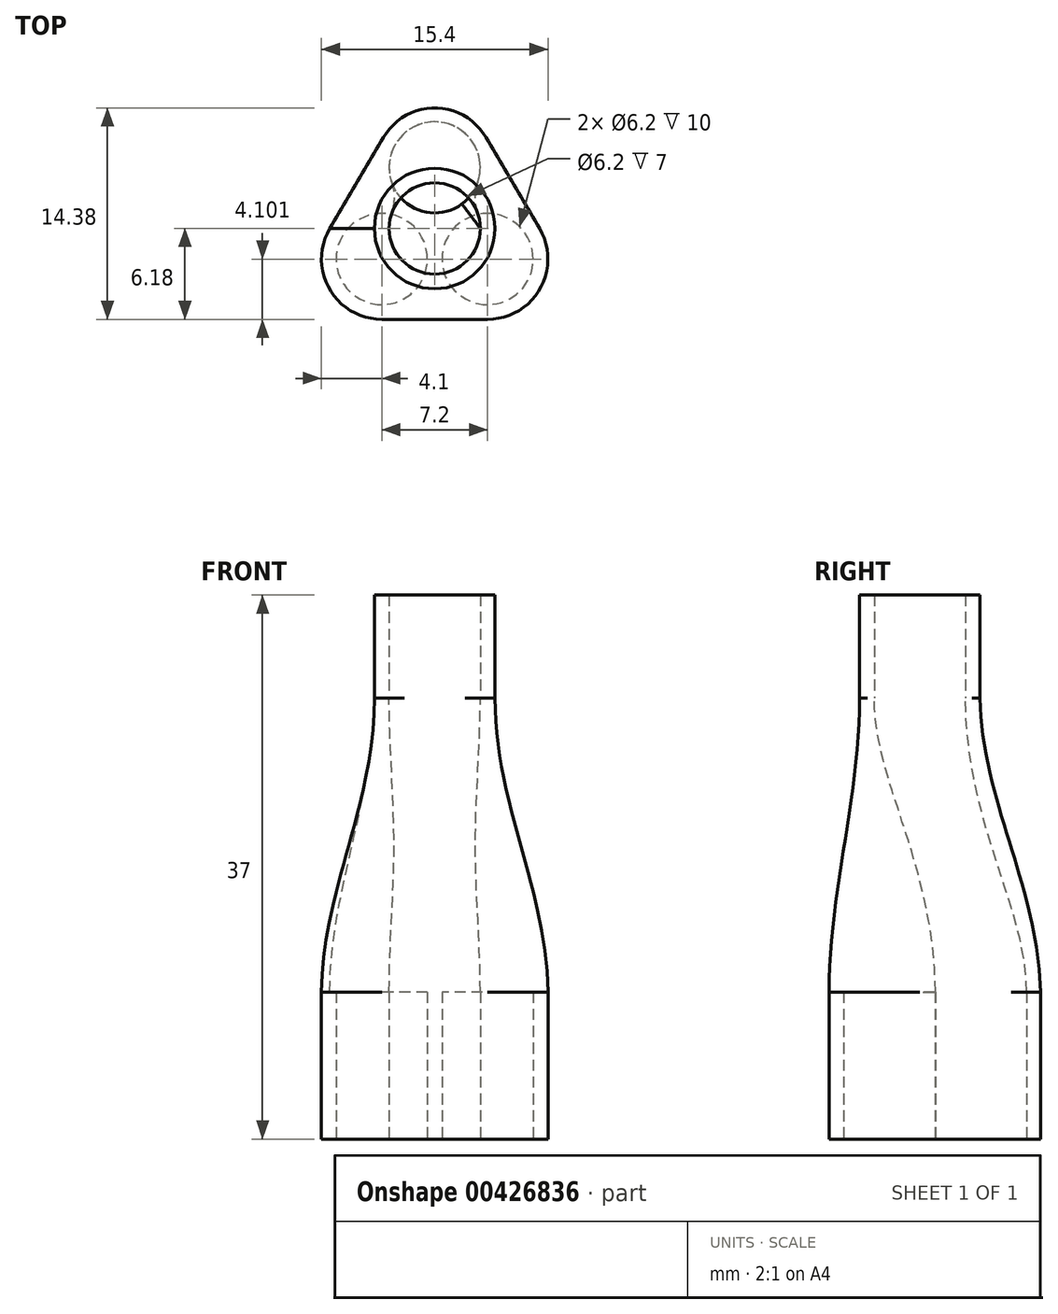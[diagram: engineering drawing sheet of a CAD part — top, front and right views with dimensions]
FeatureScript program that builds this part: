
annotation { "Feature Type Name" : "Feature", "Feature Type Description" : "" }
export const myFeature = defineFeature(function(context is Context, id is Id, definition is map)
    precondition{}
    {
        {
            var Q0;
            Q0=qCreatedBy(makeId("Top.planeOp"),FACE);
            var sketch = newSketch(context, id + "F0", { "sketchPlane" : qUnion([Q0])});
            skCircle(sketch, "E0", {"center": v(0, 4.16) * mm, "radius": 3.1 * mm});
            skCircle(sketch, "E1", {"center": v(3.6, -2.08) * mm, "radius": 3.1 * mm});
            skCircle(sketch, "E2", {"center": v(-3.6, -2.08) * mm, "radius": 3.1 * mm});
            skLineSegment(sketch, "E3", {"start": v(0, 4.16) * mm, "end": v(0, 0) * mm, "construction": true});
            skLineSegment(sketch, "E4", {"start": v(0, 0) * mm, "end": v(3.6, -2.08) * mm, "construction": true});
            skLineSegment(sketch, "E5", {"start": v(-3.6, -2.08) * mm, "end": v(0, 0) * mm, "construction": true});
            skLineSegment(sketch, "E6", {"start": v(-3.6, -2.08) * mm, "end": v(0, 4.16) * mm, "construction": true});
            skLineSegment(sketch, "E7", {"start": v(3.6, -2.08) * mm, "end": v(0, 4.16) * mm, "construction": true});
            skLineSegment(sketch, "E8", {"start": v(3.6, -2.08) * mm, "end": v(-3.6, -2.08) * mm, "construction": true});
            skPoint(sketch, "E9", {"position": v(1.55, 1.47) * mm});
            skPoint(sketch, "E10", {"position": v(2.05, 0.6) * mm});
            skLineSegment(sketch, "E11", {"start": v(-7.13, 0) * mm, "end": v(-3.48, 6.2) * mm});
            skLineSegment(sketch, "E12", {"start": v(3.48, 6.2) * mm, "end": v(7.13, 0) * mm});
            skLineSegment(sketch, "E13", {"start": v(3.6, -6.18) * mm, "end": v(-3.6, -6.18) * mm});
            skArc(sketch, "E14", {"start": v(-7.13, 0) * mm, "mid": v(-7.16, -4.11) * mm, "end": v(-3.6, -6.18) * mm});
            skArc(sketch, "E15", {"start": v(3.48, 6.2) * mm, "mid": v(0, 8.2) * mm, "end": v(-3.48, 6.2) * mm});
            skArc(sketch, "E16", {"start": v(3.6, -6.18) * mm, "mid": v(7.16, -4.11) * mm, "end": v(7.13, 0) * mm});
            skSolve(sketch);
        }
        {
            var Q0;
            Q0=makeQuery(id+"F0.imprint","IMPRINT",FACE,{"disambiguationData":[TD([[makeQuery(id+"F0.imprint","IMPRINT",EDGE,{"derivedFrom":sQuery(id+"F0.wireOp",EDGE,"E0")}),-1.0]])]});
            extrude(context, id + "F1", {"entities" : qUnion([Q0]), "depth" : 10 * mm});
        }
        {
            var Q0;
            Q0=makeQuery(id+"F1.opExtrude","CAP_FACE",FACE,{"disambiguationData":[OSD([sQuery(id+"F0.wireOp",EDGE,"E0"),sQuery(id+"F0.wireOp",EDGE,"E1"),sQuery(id+"F0.wireOp",EDGE,"E2"),sQuery(id+"F0.wireOp",EDGE,"E11"),sQuery(id+"F0.wireOp",EDGE,"E12"),sQuery(id+"F0.wireOp",EDGE,"E13"),sQuery(id+"F0.wireOp",EDGE,"E14"),sQuery(id+"F0.wireOp",EDGE,"E15"),sQuery(id+"F0.wireOp",EDGE,"E16")])],"isStart":false});
            var sketch = newSketch(context, id + "F2", { "sketchPlane" : qUnion([Q0])});
            skLineSegment(sketch, "E17.0", {"start": v(3.48, 6.2) * mm, "end": v(7.13, 0) * mm});
            skArc(sketch, "E17.1", {"start": v(3.48, 6.2) * mm, "mid": v(0, 8.2) * mm, "end": v(-3.48, 6.2) * mm});
            skLineSegment(sketch, "E17.2", {"start": v(-7.13, 0) * mm, "end": v(-3.48, 6.2) * mm});
            skArc(sketch, "E17.3", {"start": v(-7.13, 0) * mm, "mid": v(-7.16, -4.11) * mm, "end": v(-3.6, -6.18) * mm});
            skLineSegment(sketch, "E17.4", {"start": v(3.6, -6.18) * mm, "end": v(-3.6, -6.18) * mm});
            skArc(sketch, "E17.5", {"start": v(3.6, -6.18) * mm, "mid": v(7.16, -4.11) * mm, "end": v(7.13, 0) * mm});
            skSolve(sketch);
        }
        {
            var Q0;
            Q0=makeQuery(id+"F2.imprint","IMPRINT",FACE,{"disambiguationData":[TD([[makeQuery(id+"F2.imprint","IMPRINT",EDGE,{"derivedFrom":sQuery(id+"F2.wireOp",EDGE,"E17.0")}),-1.0]])]});
            cPlane(context, id + "F3", {"entities" : qUnion([Q0]), "cplaneType" : CPlaneType.OFFSET, "offset" : 20 * mm, "width" : 150 * mm, "height" : 150 * mm});
        }
        {
            var Q0;
            Q0=qCreatedBy(id+"F3.planeOp",FACE);
            var sketch = newSketch(context, id + "F4", { "sketchPlane" : qUnion([Q0])});
            skCircle(sketch, "E18", {"center": v(0, 0) * mm, "radius": 3.1 * mm, "construction": true});
            skCircle(sketch, "E19", {"center": v(0, 0) * mm, "radius": 4.1 * mm});
            skSolve(sketch);
        }
        {
            var Q1;
            Q1 = qSketchRegion(id + "F2", true);
            var Q2;
            Q2 = qSketchRegion(id + "F4", true);
            loft(context, id + "F5", {"operationType" : NewBodyOperationType.ADD, "startCondition" : LoftEndDerivativeType.NORMAL_TO_PROFILE, "startMagnitude" : 1, "endCondition" : LoftEndDerivativeType.NORMAL_TO_PROFILE, "endMagnitude" : 1, "sheetProfilesArray" : [{ "sheetProfileEntities" : qUnion([Q1]) }, { "sheetProfileEntities" : qUnion([Q2]) }]});
        }
        {
            var Q0;
            Q0=makeQuery(id+"F5.opLoft","CAP_FACE",FACE,{"disambiguationData":[OSD([makeQuery(id+"F4.imprint","IMPRINT",FACE,{"disambiguationData":[TD([[makeQuery(id+"F4.imprint","IMPRINT",EDGE,{"derivedFrom":sQuery(id+"F4.wireOp",EDGE,"E19")}),1.0]])]})])],"isStart":true});
            var sketch = newSketch(context, id + "F6", { "sketchPlane" : qUnion([Q0])});
            skCircle(sketch, "E20", {"center": v(0, 0) * mm, "radius": 3.1 * mm});
            skSolve(sketch);
        }
        {
            var Q0;
            {var subQ0=sQuery(id+"F0.wireOp",EDGE,"E2");Q0=makeQuery(id+"F5.boolean.opBoolean","SPLIT",FACE,{"disambiguationData":[TD([makeQuery(id+"F1.opExtrude","SWEPT_FACE",FACE,{"disambiguationData":[OSD([subQ0])]})])],"derivedFrom":makeQuery(id+"F5.opLoft","CAP_FACE",FACE,{"disambiguationData":[OSD([makeQuery(id+"F2.imprint","IMPRINT",FACE,{"disambiguationData":[TD([[makeQuery(id+"F2.imprint","IMPRINT",EDGE,{"derivedFrom":sQuery(id+"F2.wireOp",EDGE,"E17.0")}),-1.0]])]})])],"isStart":true})});}
            var sketch = newSketch(context, id + "F7", { "sketchPlane" : qUnion([Q0])});
            skCircle(sketch, "E21.0.0", {"center": v(0, -4.16) * mm, "radius": 3.1 * mm});
            skSolve(sketch);
        }
        {
            var Q1;
            Q1 = qSketchRegion(id + "F6", true);
            var Q2;
            Q2 = qSketchRegion(id + "F7", true);
            loft(context, id + "F8", {"operationType" : NewBodyOperationType.REMOVE, "startCondition" : LoftEndDerivativeType.NORMAL_TO_PROFILE, "startMagnitude" : 1, "endCondition" : LoftEndDerivativeType.NORMAL_TO_PROFILE, "endMagnitude" : 1, "sheetProfilesArray" : [{ "sheetProfileEntities" : qUnion([Q1]) }, { "sheetProfileEntities" : qUnion([Q2]) }]});
        }
        {
            var Q0;
            Q0=qCreatedBy(makeId("Right.planeOp"),FACE);
            var sketch = newSketch(context, id + "F9", { "sketchPlane" : qUnion([Q0])});
            skLineSegment(sketch, "E22", {"start": v(0, 0) * mm, "end": v(0, 38.85) * mm, "construction": true});
            skSolve(sketch);
        }
        {
            var Q0;
            Q0=makeQuery(id+"F4.imprint","IMPRINT",FACE,{"disambiguationData":[TD([[makeQuery(id+"F4.imprint","IMPRINT",EDGE,{"derivedFrom":sQuery(id+"F4.wireOp",EDGE,"E19")}),1.0]])]});
            var sketch = newSketch(context, id + "F10", { "sketchPlane" : qUnion([Q0])});
            skCircle(sketch, "E23.0", {"center": v(0, 0) * mm, "radius": 3.1 * mm});
            skCircle(sketch, "E23.1", {"center": v(0, 0) * mm, "radius": 4.1 * mm});
            skSolve(sketch);
        }
        {
            var Q0;
            Q0 = qSketchRegion(id + "F10", true);
            extrude(context, id + "F11", {"entities" : qUnion([Q0]), "operationType" : NewBodyOperationType.ADD, "depth" : 7 * mm});
        }
    });
